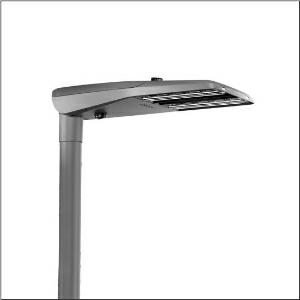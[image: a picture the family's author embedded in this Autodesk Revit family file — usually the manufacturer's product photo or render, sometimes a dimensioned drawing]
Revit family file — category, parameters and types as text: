
# Revit family: streetlight_sl_11_iq_midi___pc-l_5xc3e51y08me_36d5
name_source: partatom
category: Lighting Fixtures
units: mm (PartAtom-declared; Revit-internal decimal feet)

## family parameters
Cut with Voids When Loaded = No
Host = Face
Light Source = No
Part Type = Normal
Room Calculation Point = No
Round Connector Dimension = Use Diameter
Shared = No

## types (1)
- --- (1 x LED, 15540 lm, 122.7 W, 3000K)
    Apparent Load = 123 VA
    CIE Flux Codes = 37 73 96 100 100
    Color Rendering = 70
    Color Temperature = 3000K
    Default Elevation = 1800 mm
    Description = Streetlight SL 11 iQ midi, mast luminaire, primary light control with 3 zone facetted reflector, of plastic, silver coated, highly specular, primary optical cover: cover, of PMMA, transparent, light distribution: PC-L, light emission: direct distribution, primary light characteristic: asymmetric, left, installation type: post-top, side-entry, lamps: LED, High Power LED, rated values: 15.540lm | 122,7W | 126,7lm/W (begin service life); end service life: 15.540lm | 130,2W; at 50% lumin. flux: 7.770lm | 56,1W | 138,5lm/W, colour temperature: 3000K, colour rendering: CRI > 70, light colour: 730, light setting 1 begin service life: 100% | 15.540lm | 122,7W | 126,7lm/W | 3.000K, light setting 1 end service life: 130,2W, further light settings possible, control: pre-setting: logarithmic dimming characteristic, Street-Remote, Auto-Match, Temp-Guard, Lumen-Switch, Night-Set, Smart-Wire, Light-Fading, Desk-Remote (wireless, voltage-free reading and setting of iQ features in the workshop via application-optimized NFC function/RFID function), optimised constant luminous flux control (CLO 2.0), with cable H07RN-F 3x 1.5mm², mains connection: 230..240V, AC, 50/60Hz, connection cable pre-assembled, cable length: 12,5m, luminaire housing, of diecast aluminium, powder-coated, SITECO metallic grey (DB 702S), please order mast flange separately, inclination adjustable without tools: 0°, 5°, 10°, 15° (post-top) | 0°, -5°, -10°, -15° (side-entry), sealing non-destructively replaceable, multi-level sealing system, length: 780mm, width: 376mm, height: 118mm, mast flange for spigot size: 42mm (side-entry): 5XC10008XM4, 60/48mm (side-entry/post-top): 5XC10108XM2, 76/60mm (side-entry/post-top): 5XC10108XM1, equipment: Power, Smart Interface below and above, protection rating (complete): IP66, insulation class (complete): insulation class II (safety insulation), certification: CE, ENEC, ENEC+, VDE, UKCA, impact resistance: IK10, permissible operating ambient temperature for outdoor applications: -25..+50°C, standard-compliant lighting for roads and squares, Environmental Product Declaration (EPD) tested and certified by an independent institute, packaging unit: 1 piece

Light Distribution: PC-L
    Height = 118 mm
    Lamp = 1 x LED
    Lamp Light Flux = 15540 lm
    Lamp Power = 122.7 W
    Lamp count = 1
    Length = 780 mm
    Luminous efficacy = 127 lm/W
    Manufacturer = Siteco
    ModVariant = No
    Model = 5XC3E51Y08ME
    Number of Poles = 1
    OnlyDefault = Yes
    Power Factor = 1
    Product Name = Streetlight SL 11 iQ midi | PC-L
    Product group = mast luminaire | pylon top
    ProductGroupID = 6100
    Protection Class = Protection class II
    Protection Degree = IP 66
    RLX_Detail_Level = 1
    RLX_Emergency_Light_Flux = 0 lm
    RLX_Emergency_Type = 0
    RLX_Emergency_Type_DB = No
    RlxData = <blob elided: 73745 chars, md5=02fe0274>
    Socket = socket
    Standby Power = 0 W
    System Light Flux = 15540 lm
    System Power = 123 W
    Type Comments = factory setting: luminous flux: 100 % | dim-lin: 254 | 552 mA
    Type Image = l_1004429.jpg
    URL = http://relux.com
    VarID = @adj_132537
    Voltage = 0 V
    Weight = 0.00 kg
    Width = 376 mm

## geometry (parser evidence)
native form markers: Blend x4, Sweep x10
no freeform markers — native parametric forms only
